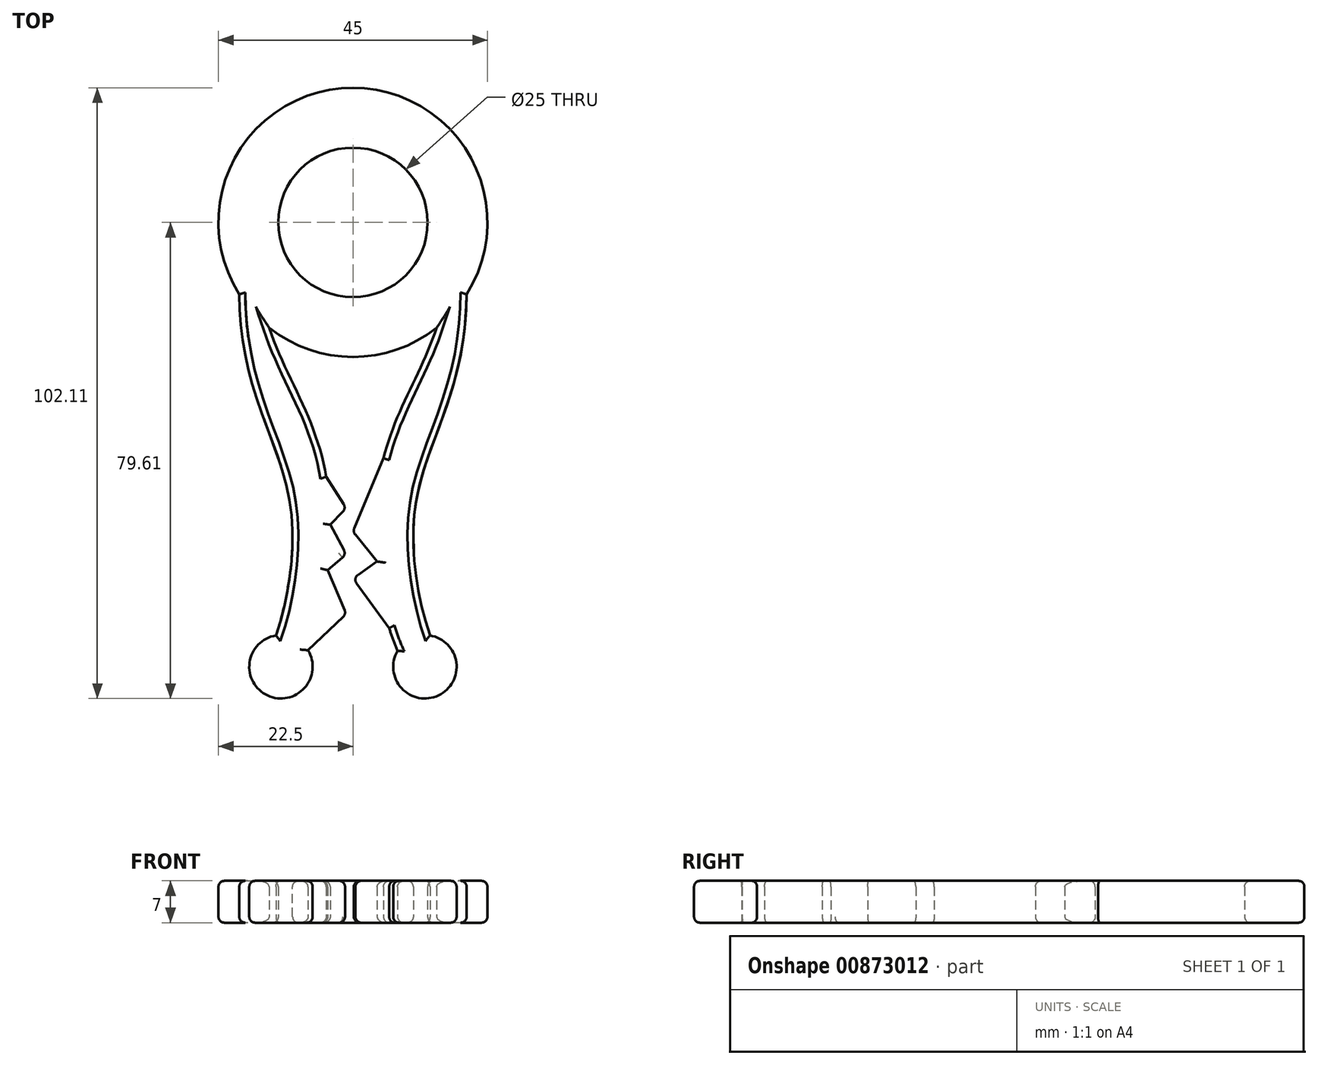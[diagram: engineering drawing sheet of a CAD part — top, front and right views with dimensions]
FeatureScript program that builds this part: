
annotation { "Feature Type Name" : "Feature", "Feature Type Description" : "" }
export const myFeature = defineFeature(function(context is Context, id is Id, definition is map)
    precondition{}
    {
        {
            var Q0;
            Q0=qCreatedBy(makeId("Top.planeOp"),FACE);
            var sketch = newSketch(context, id + "F0", { "sketchPlane" : qUnion([Q0])});
            skCircle(sketch, "E0", {"center": v(0, 0) * mm, "radius": 12.5 * mm});
            skCircle(sketch, "E1", {"center": v(0, 0) * mm, "radius": 22.5 * mm});
            skFitSpline(sketch, "E2", {"points": [v(-19.02, -12.02) * mm, v(-10.33, -48.27) * mm, v(-15.56, -74.84) * mm], "startDerivative": vector(1.05, -95.35) * mm, "endDerivative": vector(-20.96, -31.25) * mm});
            skFitSpline(sketch, "E3.0", {"points": [v(-16.18, -6.89) * mm, v(-16.01, -8.6) * mm, v(-15.55, -11.78) * mm, v(-14.54, -15.92) * mm, v(-13.28, -19.64) * mm, v(-11.81, -23.15) * mm, v(-10.2, -26.61) * mm, v(-8.5, -30.2) * mm, v(-7.1, -33.44) * mm, v(-6.07, -36.24) * mm, v(-5.38, -38.45) * mm, v(-4.89, -40.4) * mm, v(-4.56, -42.02) * mm, v(-4.28, -43.65) * mm, v(-4.02, -45.69) * mm, v(-3.78, -48.96) * mm, v(-3.76, -53.02) * mm, v(-4.1, -57.78) * mm, v(-4.76, -62.32) * mm, v(-5.7, -66.54) * mm, v(-6.7, -69.75) * mm, v(-7.68, -72.13) * mm, v(-8.24, -73.28) * mm, v(-8.56, -73.85) * mm]});
            skFitSpline(sketch, "E4.MirrorCS", {"points": [v(16.18, -6.89) * mm, v(16.01, -8.6) * mm, v(15.55, -11.78) * mm, v(14.54, -15.92) * mm, v(13.28, -19.64) * mm, v(11.81, -23.15) * mm, v(10.2, -26.61) * mm, v(8.5, -30.2) * mm, v(7.1, -33.44) * mm, v(6.07, -36.24) * mm, v(5.38, -38.45) * mm, v(4.89, -40.4) * mm, v(4.56, -42.02) * mm, v(4.28, -43.65) * mm, v(4.02, -45.69) * mm, v(3.78, -48.96) * mm, v(3.76, -53.02) * mm, v(4.1, -57.78) * mm, v(4.76, -62.32) * mm, v(5.7, -66.54) * mm, v(6.7, -69.75) * mm, v(7.68, -72.13) * mm, v(8.24, -73.28) * mm, v(8.56, -73.85) * mm]});
            skFitSpline(sketch, "E5.MirrorCS", {"points": [v(19.02, -12.02) * mm, v(10.33, -48.27) * mm, v(15.56, -74.84) * mm], "startDerivative": vector(-1.05, -95.35) * mm, "endDerivative": vector(20.96, -31.25) * mm});
            skArc(sketch, "E6", {"start": v(-12.9, -69.08) * mm, "mid": v(-14.26, -79.13) * mm, "end": v(-7.51, -71.55) * mm});
            skArc(sketch, "E7.MirrorC", {"start": v(12.9, -69.08) * mm, "mid": v(14.3, -79.1) * mm, "end": v(7.47, -71.62) * mm});
            skLineSegment(sketch, "E8", {"start": v(-4.48, -42.5) * mm, "end": v(-1.13, -47.79) * mm});
            skLineSegment(sketch, "E9", {"start": v(-1.13, -47.79) * mm, "end": v(-3.79, -50.55) * mm});
            skLineSegment(sketch, "E10", {"start": v(-3.79, -50.55) * mm, "end": v(-1.13, -55.51) * mm});
            skLineSegment(sketch, "E11", {"start": v(-1.13, -55.51) * mm, "end": v(-4.2, -58.16) * mm});
            skLineSegment(sketch, "E12", {"start": v(-4.2, -58.16) * mm, "end": v(-1.13, -65.48) * mm});
            skLineSegment(sketch, "E13", {"start": v(-1.13, -65.48) * mm, "end": v(-7.51, -71.55) * mm});
            skLineSegment(sketch, "E14", {"start": v(5.17, -39.3) * mm, "end": v(0, -51.74) * mm});
            skLineSegment(sketch, "E15", {"start": v(0, -51.74) * mm, "end": v(4.05, -56.7) * mm});
            skLineSegment(sketch, "E16", {"start": v(4.05, -56.7) * mm, "end": v(0, -59.52) * mm});
            skLineSegment(sketch, "E17", {"start": v(0, -59.52) * mm, "end": v(6.16, -67.97) * mm});
            skPoint(sketch, "E18.orphan", {"position": v(-8.52, -73.78) * mm});
            skFitSpline(sketch, "E19.trimOffspring", {"points": [v(16.18, -6.89) * mm, v(16.01, -8.6) * mm, v(15.55, -11.78) * mm, v(14.54, -15.92) * mm, v(13.28, -19.64) * mm, v(11.81, -23.15) * mm, v(10.2, -26.61) * mm, v(8.5, -30.2) * mm, v(7.1, -33.44) * mm, v(6.07, -36.24) * mm, v(5.38, -38.45) * mm, v(4.89, -40.4) * mm, v(4.56, -42.02) * mm, v(4.28, -43.65) * mm, v(4.02, -45.69) * mm, v(3.78, -48.96) * mm, v(3.76, -53.02) * mm, v(4.1, -57.78) * mm, v(4.76, -62.32) * mm, v(5.7, -66.54) * mm, v(6.7, -69.75) * mm, v(7.68, -72.13) * mm, v(8.24, -73.28) * mm, v(8.56, -73.85) * mm]});
            skPoint(sketch, "E20.orphan", {"position": v(8.52, -73.78) * mm});
            skSolve(sketch);
        }
        {
            var Q0;
            Q0=makeQuery(id+"F0.imprint","IMPRINT",FACE,{"disambiguationData":[TD([[makeQuery(id+"F0.imprint","IMPRINT",EDGE,{"derivedFrom":sQuery(id+"F0.wireOp",EDGE,"E0")}),-1.0]])]});
            extrude(context, id + "F1", {"entities" : qUnion([Q0]), "endBound" : BoundingType.SYMMETRIC, "depth" : 7 * mm, "offsetDistance" : 25 * mm});
        }
        {
            var Q0;
            {var subQ0=sQuery(id+"F0.wireOp",EDGE,"E4.MirrorCS");var subQ4=sQuery(id+"F0.wireOp",EDGE,"E1");var subQ5=makeQuery(id+"F0.imprint","INTERSECT",VERTEX,{"derivedFrom":[subQ4,subQ0]});Q0=makeQuery(id+"F0.imprint","IMPRINT",FACE,{"disambiguationData":[TD([[makeQuery(id+"F0.imprint","IMPRINT",EDGE,{"disambiguationData":[TD([[subQ5,-1.0]])],"derivedFrom":subQ4}),-1.0]])]});}
            var Q1;
            {var subQ3=sQuery(id+"F0.wireOp",EDGE,"E1");var subQ5=sQuery(id+"F0.wireOp",EDGE,"E2");var subQ6=makeQuery(id+"F0.imprint","INTERSECT",VERTEX,{"derivedFrom":[subQ3,subQ5]});Q1=makeQuery(id+"F0.imprint","IMPRINT",FACE,{"disambiguationData":[TD([[makeQuery(id+"F0.imprint","IMPRINT",EDGE,{"disambiguationData":[TD([[subQ6,-1.0]])],"derivedFrom":subQ3}),-1.0]])]});}
            var Q2;
            {var subQ0=sQuery(id+"F0.wireOp",EDGE,"E8");Q2=makeQuery(id+"F0.imprint","IMPRINT",FACE,{"disambiguationData":[TD([[makeQuery(id+"F0.imprint","IMPRINT",EDGE,{"derivedFrom":subQ0}),-1.0]])]});}
            var Q3;
            {var subQ0=sQuery(id+"F0.wireOp",EDGE,"E10");Q3=makeQuery(id+"F0.imprint","IMPRINT",FACE,{"disambiguationData":[TD([[makeQuery(id+"F0.imprint","IMPRINT",EDGE,{"derivedFrom":subQ0}),-1.0]])]});}
            var Q4;
            {var subQ0=sQuery(id+"F0.wireOp",EDGE,"E12");Q4=makeQuery(id+"F0.imprint","IMPRINT",FACE,{"disambiguationData":[TD([[makeQuery(id+"F0.imprint","IMPRINT",EDGE,{"derivedFrom":subQ0}),-1.0]])]});}
            var Q5;
            {var subQ0=sQuery(id+"F0.wireOp",EDGE,"E16");Q5=makeQuery(id+"F0.imprint","IMPRINT",FACE,{"disambiguationData":[TD([[makeQuery(id+"F0.imprint","IMPRINT",EDGE,{"derivedFrom":subQ0}),1.0]])]});}
            var Q6;
            {var subQ0=sQuery(id+"F0.wireOp",EDGE,"E14");Q6=makeQuery(id+"F0.imprint","IMPRINT",FACE,{"disambiguationData":[TD([[makeQuery(id+"F0.imprint","IMPRINT",EDGE,{"derivedFrom":subQ0}),1.0]])]});}
            var Q7;
            {var subQ0=sQuery(id+"F0.wireOp",EDGE,"08bba9fe-ce6f-4a78-b5c7-c6d0d5e268800.MirrorCS");Q7=makeQuery(id+"F0.imprint","IMPRINT",FACE,{"disambiguationData":[TD([[makeQuery(id+"F0.imprint","IMPRINT",EDGE,{"derivedFrom":subQ0}),1.0]])]});}
            var Q8;
            {var subQ0=sQuery(id+"F0.wireOp",EDGE,"08bba9fe-ce6f-4a78-b5c7-c6d0d5e268800.MirrorCS");Q8=makeQuery(id+"F0.imprint","IMPRINT",FACE,{"disambiguationData":[TD([[makeQuery(id+"F0.imprint","IMPRINT",EDGE,{"derivedFrom":subQ0}),-1.0]])]});}
            var Q9;
            {var subQ5=sQuery(id+"F0.wireOp",EDGE,"XkcnYsRi-8ppW-bxOu-Q17c-T6rpAmNDpced");Q9=makeQuery(id+"F0.imprint","IMPRINT",FACE,{"disambiguationData":[TD([[makeQuery(id+"F0.imprint","IMPRINT",EDGE,{"derivedFrom":subQ5}),-1.0]])]});}
            extrude(context, id + "F2", {"entities" : qUnion([Q0, Q1, Q2, Q3, Q4, Q5, Q6, Q7, Q8, Q9]), "operationType" : NewBodyOperationType.ADD, "endBound" : BoundingType.SYMMETRIC, "depth" : 7 * mm, "offsetDistance" : 25 * mm});
        }
        {
            var Q0;
            {var subQ0=sQuery(id+"F0.wireOp",EDGE,"E1");Q0=makeQuery(id+"F2.boolean.opBoolean","MERGE",FACE,{"derivedFrom":[makeQuery(id+"F1.opExtrude","CAP_FACE",FACE,{"disambiguationData":[OSD([sQuery(id+"F0.wireOp",EDGE,"E0"),subQ0])],"isStart":true}),makeQuery(id+"F2.opExtrude","CAP_FACE",FACE,{"disambiguationData":[OSD([subQ0,sQuery(id+"F0.wireOp",EDGE,"E2"),sQuery(id+"F0.wireOp",EDGE,"E3.0"),sQuery(id+"F0.wireOp",EDGE,"E6"),sQuery(id+"F0.wireOp",EDGE,"E8"),sQuery(id+"F0.wireOp",EDGE,"E9"),sQuery(id+"F0.wireOp",EDGE,"E10"),sQuery(id+"F0.wireOp",EDGE,"E11"),sQuery(id+"F0.wireOp",EDGE,"E12"),sQuery(id+"F0.wireOp",EDGE,"E13")])],"isStart":true}),makeQuery(id+"F2.opExtrude","CAP_FACE",FACE,{"disambiguationData":[OSD([subQ0,sQuery(id+"F0.wireOp",EDGE,"E4.MirrorCS"),sQuery(id+"F0.wireOp",EDGE,"E5.MirrorCS"),sQuery(id+"F0.wireOp",EDGE,"E7.MirrorC"),sQuery(id+"F0.wireOp",EDGE,"E14"),sQuery(id+"F0.wireOp",EDGE,"E15"),sQuery(id+"F0.wireOp",EDGE,"E16"),sQuery(id+"F0.wireOp",EDGE,"E17"),sQuery(id+"F0.wireOp",EDGE,"E19.trimOffspring")])],"isStart":true})]});}
            var Q1;
            {var subQ0=sQuery(id+"F0.wireOp",EDGE,"E1");Q1=makeQuery(id+"F2.boolean.opBoolean","MERGE",FACE,{"derivedFrom":[makeQuery(id+"F1.opExtrude","CAP_FACE",FACE,{"disambiguationData":[OSD([sQuery(id+"F0.wireOp",EDGE,"E0"),subQ0])],"isStart":false}),makeQuery(id+"F2.opExtrude","CAP_FACE",FACE,{"disambiguationData":[OSD([subQ0,sQuery(id+"F0.wireOp",EDGE,"E2"),sQuery(id+"F0.wireOp",EDGE,"E3.0"),sQuery(id+"F0.wireOp",EDGE,"E6"),sQuery(id+"F0.wireOp",EDGE,"E8"),sQuery(id+"F0.wireOp",EDGE,"E9"),sQuery(id+"F0.wireOp",EDGE,"E10"),sQuery(id+"F0.wireOp",EDGE,"E11"),sQuery(id+"F0.wireOp",EDGE,"E12"),sQuery(id+"F0.wireOp",EDGE,"E13")])],"isStart":false}),makeQuery(id+"F2.opExtrude","CAP_FACE",FACE,{"disambiguationData":[OSD([subQ0,sQuery(id+"F0.wireOp",EDGE,"E4.MirrorCS"),sQuery(id+"F0.wireOp",EDGE,"E5.MirrorCS"),sQuery(id+"F0.wireOp",EDGE,"E7.MirrorC"),sQuery(id+"F0.wireOp",EDGE,"E14"),sQuery(id+"F0.wireOp",EDGE,"E15"),sQuery(id+"F0.wireOp",EDGE,"E16"),sQuery(id+"F0.wireOp",EDGE,"E17"),sQuery(id+"F0.wireOp",EDGE,"E19.trimOffspring")])],"isStart":false})]});}
            var Q2;
            Q2=makeQuery(id+"F2.opExtrude","SWEPT_EDGE",EDGE,{"disambiguationData":[OSD([sQuery(id+"F0.wireOp",EDGE,"E8"),sQuery(id+"F0.wireOp",EDGE,"E9")])]});
            var Q3;
            Q3=makeQuery(id+"F2.opExtrude","SWEPT_EDGE",EDGE,{"disambiguationData":[OSD([sQuery(id+"F0.wireOp",EDGE,"E10"),sQuery(id+"F0.wireOp",EDGE,"E11")])]});
            var Q4;
            Q4=makeQuery(id+"F2.opExtrude","SWEPT_EDGE",EDGE,{"disambiguationData":[OSD([sQuery(id+"F0.wireOp",EDGE,"E12"),sQuery(id+"F0.wireOp",EDGE,"E13")])]});
            var Q5;
            Q5=makeQuery(id+"F2.opExtrude","SWEPT_EDGE",EDGE,{"disambiguationData":[OSD([sQuery(id+"F0.wireOp",EDGE,"E16"),sQuery(id+"F0.wireOp",EDGE,"E17")])]});
            var Q6;
            Q6=makeQuery(id+"F2.opExtrude","SWEPT_EDGE",EDGE,{"disambiguationData":[OSD([sQuery(id+"F0.wireOp",EDGE,"E14"),sQuery(id+"F0.wireOp",EDGE,"E15")])]});
            fillet(context, id + "F3", {"entities" : qUnion([Q0, Q1, Q2, Q3, Q4, Q5, Q6]), "radius" : 1 * mm, "tangentPropagation" : true, "allowEdgeOverflow" : false});
        }
    });
